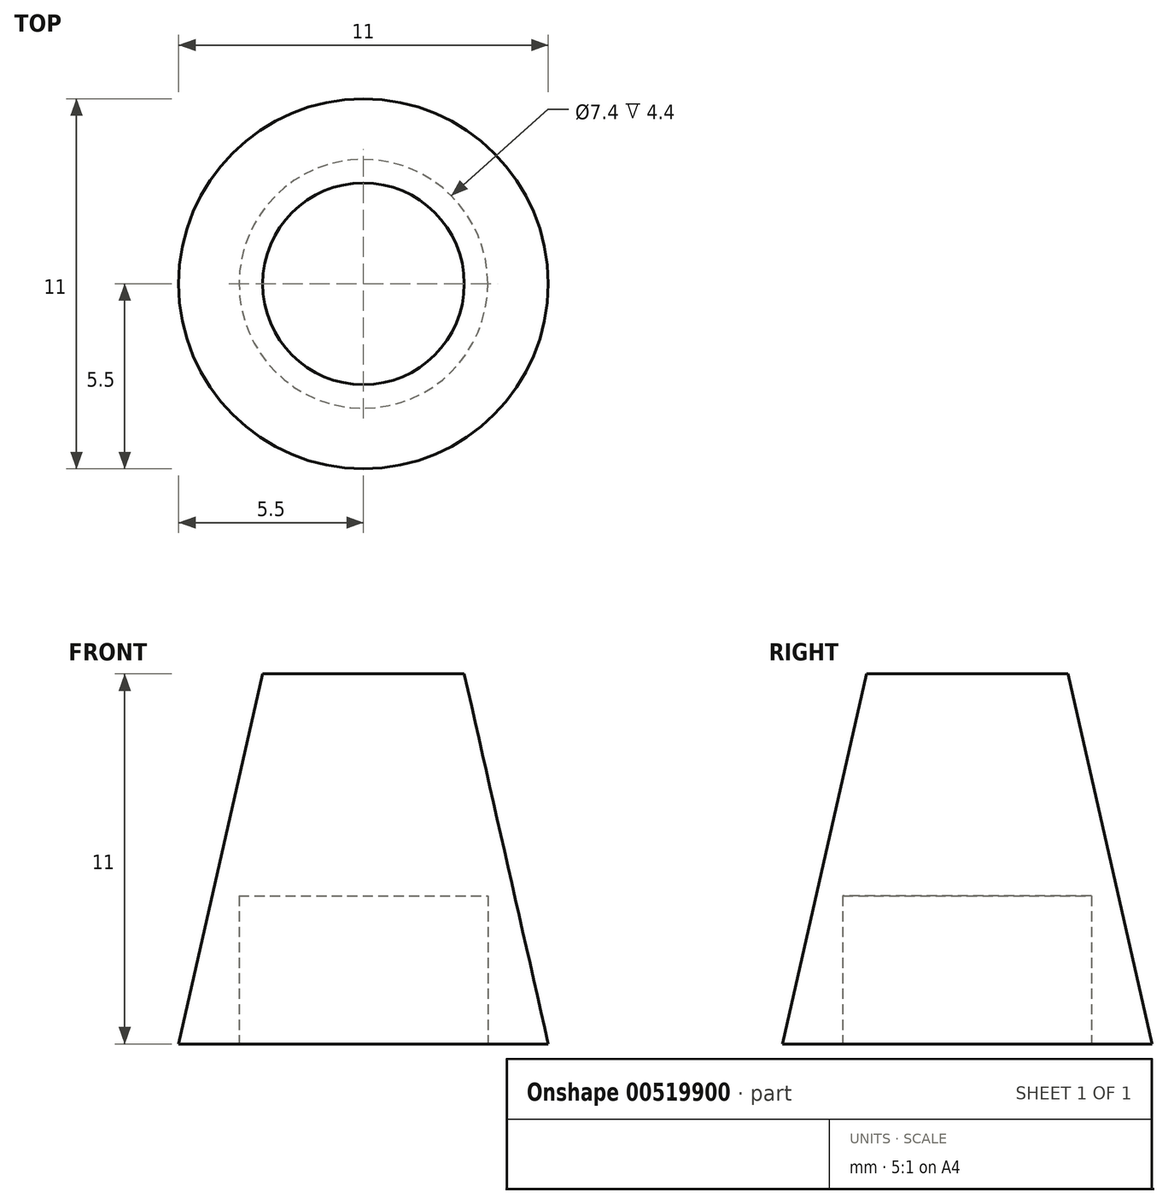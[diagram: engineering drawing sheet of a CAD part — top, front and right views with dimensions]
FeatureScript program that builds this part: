
annotation { "Feature Type Name" : "Feature", "Feature Type Description" : "" }
export const myFeature = defineFeature(function(context is Context, id is Id, definition is map)
    precondition{}
    {
        {
            var Q0;
            Q0=qCreatedBy(makeId("Front.planeOp"),FACE);
            var sketch = newSketch(context, id + "F0", { "sketchPlane" : qUnion([Q0])});
            skLineSegment(sketch, "E0", {"start": v(0, 0) * mm, "end": v(0, 11) * mm});
            skLineSegment(sketch, "E1", {"start": v(0, 0) * mm, "end": v(5.5, 0) * mm});
            skLineSegment(sketch, "E2", {"start": v(0, 17.17) * mm, "end": v(0, -6.48) * mm, "construction": true});
            skPoint(sketch, "E2.endSnap0", {"position": v(0, 5.5) * mm});
            skLineSegment(sketch, "E3", {"start": v(0, 11) * mm, "end": v(3, 11) * mm});
            skLineSegment(sketch, "E4", {"start": v(3, 11) * mm, "end": v(5.5, 0) * mm});
            skSolve(sketch);
        }
        {
            var Q0;
            Q0=makeQuery(id+"F0.imprint","IMPRINT",FACE,{"disambiguationData":[TD([[makeQuery(id+"F0.imprint","IMPRINT",EDGE,{"derivedFrom":sQuery(id+"F0.wireOp",EDGE,"E0")}),-1.0]])]});
            var Q1;
            Q1=sQuery(id+"F0.wireOp",EDGE,"E2");
            revolve(context, id + "F1", {"entities" : qUnion([Q0]), "axis" : qUnion([Q1]), "revolveType" : RevolveType.FULL});
        }
        {
            var Q0;
            Q0=makeQuery(id+"F1.opRevolve","SWEPT_FACE",FACE,{"disambiguationData":[OSD([sQuery(id+"F0.wireOp",EDGE,"E1")])]});
            var sketch = newSketch(context, id + "F2", { "sketchPlane" : qUnion([Q0])});
            skCircle(sketch, "E5", {"center": v(0, 0) * mm, "radius": 3.7 * mm});
            skSolve(sketch);
        }
        {
            var Q0;
            Q0=makeQuery(id+"F2.imprint","IMPRINT",FACE,{"disambiguationData":[TD([[makeQuery(id+"F2.imprint","IMPRINT",EDGE,{"derivedFrom":sQuery(id+"F2.wireOp",EDGE,"E5")}),1.0]])]});
            extrude(context, id + "F3", {"entities" : qUnion([Q0]), "operationType" : NewBodyOperationType.REMOVE, "oppositeDirection" : true, "depth" : 4.4 * mm, "offsetDistance" : 25 * mm});
        }
    });
